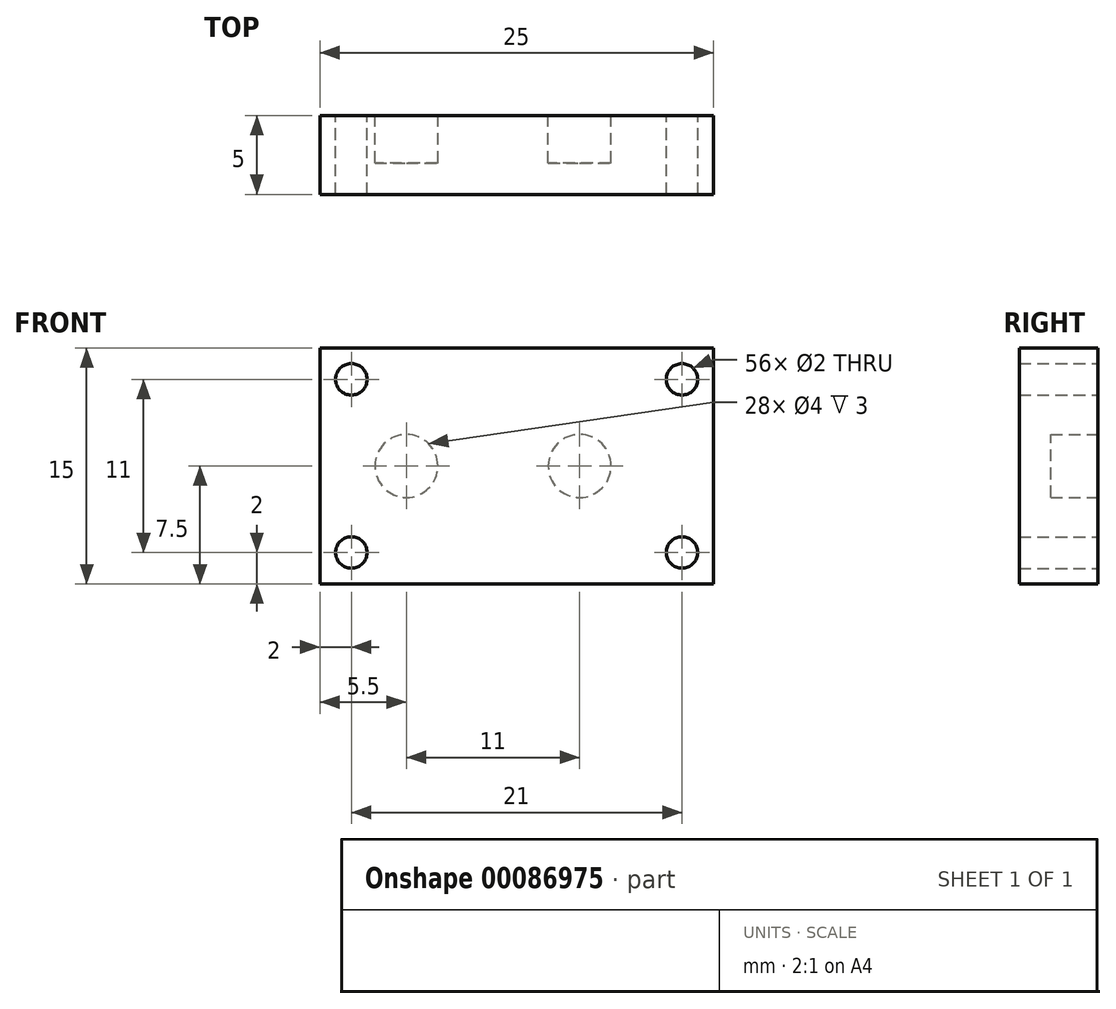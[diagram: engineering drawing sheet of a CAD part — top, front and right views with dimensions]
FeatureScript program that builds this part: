
annotation { "Feature Type Name" : "Feature", "Feature Type Description" : "" }
export const myFeature = defineFeature(function(context is Context, id is Id, definition is map)
    precondition{}
    {
        {
            var Q0;
            Q0=qCreatedBy(makeId("Front.planeOp"),FACE);
            var sketch = newSketch(context, id + "F0", { "sketchPlane" : qUnion([Q0])});
            skLineSegment(sketch, "E0.bottom", {"start": v(12.5, -7.5) * mm, "end": v(-12.5, -7.5) * mm});
            skLineSegment(sketch, "E0.top", {"start": v(12.5, 7.5) * mm, "end": v(-12.5, 7.5) * mm});
            skLineSegment(sketch, "E0.left", {"start": v(12.5, -7.5) * mm, "end": v(12.5, 7.5) * mm});
            skLineSegment(sketch, "E0.right", {"start": v(-12.5, -7.5) * mm, "end": v(-12.5, 7.5) * mm});
            skPoint(sketch, "E0.middle", {"position": v(0, 0) * mm});
            skCircle(sketch, "E1", {"center": v(-7, 0) * mm, "radius": 0.5 * mm});
            skCircle(sketch, "E2", {"center": v(4, 0) * mm, "radius": 0.5 * mm});
            skLineSegment(sketch, "E3", {"start": v(-7, 0) * mm, "end": v(4, 0) * mm});
            skCircle(sketch, "E4", {"center": v(-7, 0) * mm, "radius": 2 * mm});
            skCircle(sketch, "E5", {"center": v(4, 0) * mm, "radius": 2 * mm});
            skLineSegment(sketch, "E6.bottom", {"start": v(-10.5, 5.5) * mm, "end": v(10.5, 5.5) * mm, "construction": true});
            skLineSegment(sketch, "E6.top", {"start": v(-10.5, -5.5) * mm, "end": v(10.5, -5.5) * mm, "construction": true});
            skLineSegment(sketch, "E6.left", {"start": v(-10.5, 5.5) * mm, "end": v(-10.5, -5.5) * mm, "construction": true});
            skLineSegment(sketch, "E6.right", {"start": v(10.5, 5.5) * mm, "end": v(10.5, -5.5) * mm, "construction": true});
            skCircle(sketch, "E7", {"center": v(-10.5, 5.5) * mm, "radius": 1 * mm});
            skCircle(sketch, "E8", {"center": v(-10.5, -5.5) * mm, "radius": 1 * mm});
            skCircle(sketch, "E9", {"center": v(10.5, -5.5) * mm, "radius": 1 * mm});
            skCircle(sketch, "E10", {"center": v(10.5, 5.5) * mm, "radius": 1 * mm});
            skSolve(sketch);
        }
        {
            var Q0;
            Q0=makeQuery(id+"F0.imprint","IMPRINT",FACE,{"disambiguationData":[TD([[makeQuery(id+"F0.imprint","IMPRINT",EDGE,{"derivedFrom":sQuery(id+"F0.wireOp",EDGE,"E0.bottom")}),-1.0]])]});
            var Q1;
            Q1=makeQuery(id+"F0.imprint","IMPRINT",FACE,{"disambiguationData":[TD([[makeQuery(id+"F0.imprint","IMPRINT",EDGE,{"derivedFrom":sQuery(id+"F0.wireOp",EDGE,"E1")}),-1.0]])]});
            var Q2;
            Q2=makeQuery(id+"F0.imprint","IMPRINT",FACE,{"disambiguationData":[TD([[makeQuery(id+"F0.imprint","IMPRINT",EDGE,{"derivedFrom":sQuery(id+"F0.wireOp",EDGE,"E1")}),1.0]])]});
            var Q3;
            Q3=makeQuery(id+"F0.imprint","IMPRINT",FACE,{"disambiguationData":[TD([[makeQuery(id+"F0.imprint","IMPRINT",EDGE,{"derivedFrom":sQuery(id+"F0.wireOp",EDGE,"E2")}),1.0]])]});
            var Q4;
            Q4=makeQuery(id+"F0.imprint","IMPRINT",FACE,{"disambiguationData":[TD([[makeQuery(id+"F0.imprint","IMPRINT",EDGE,{"derivedFrom":sQuery(id+"F0.wireOp",EDGE,"E2")}),-1.0]])]});
            var Q5;
            Q5=sQuery(id+"F0.wireOp",EDGE,"E0.bottom");
            var Q6;
            Q6=sQuery(id+"F0.wireOp",EDGE,"E0.top");
            var Q7;
            Q7=sQuery(id+"F0.wireOp",EDGE,"E0.left");
            var Q8;
            Q8=sQuery(id+"F0.wireOp",EDGE,"E0.right");
            var Q9;
            Q9=sQuery(id+"F0.wireOp",EDGE,"E7");
            var Q10;
            Q10=sQuery(id+"F0.wireOp",EDGE,"E8");
            var Q11;
            Q11=sQuery(id+"F0.wireOp",EDGE,"E9");
            var Q12;
            Q12=sQuery(id+"F0.wireOp",EDGE,"E10");
            extrude(context, id + "F1", {"entities" : qUnion([Q0, Q1, Q2, Q3, Q4]), "surfaceEntities" : qUnion([Q5, Q6, Q7, Q8, Q9, Q10, Q11, Q12]), "depth" : 5 * mm});
        }
        {
            var Q0;
            Q0=makeQuery(id+"F0.imprint","IMPRINT",FACE,{"disambiguationData":[TD([[makeQuery(id+"F0.imprint","IMPRINT",EDGE,{"derivedFrom":sQuery(id+"F0.wireOp",EDGE,"E1")}),-1.0]])]});
            var Q1;
            Q1=makeQuery(id+"F0.imprint","IMPRINT",FACE,{"disambiguationData":[TD([[makeQuery(id+"F0.imprint","IMPRINT",EDGE,{"derivedFrom":sQuery(id+"F0.wireOp",EDGE,"E2")}),-1.0]])]});
            var Q2;
            Q2=makeQuery(id+"F0.imprint","IMPRINT",FACE,{"disambiguationData":[TD([[makeQuery(id+"F0.imprint","IMPRINT",EDGE,{"derivedFrom":sQuery(id+"F0.wireOp",EDGE,"E2")}),1.0]])]});
            var Q3;
            Q3=makeQuery(id+"F0.imprint","IMPRINT",FACE,{"disambiguationData":[TD([[makeQuery(id+"F0.imprint","IMPRINT",EDGE,{"derivedFrom":sQuery(id+"F0.wireOp",EDGE,"E1")}),1.0]])]});
            extrude(context, id + "F2", {"entities" : qUnion([Q0, Q1, Q2, Q3]), "operationType" : NewBodyOperationType.REMOVE, "depth" : 3 * mm});
        }
    });
